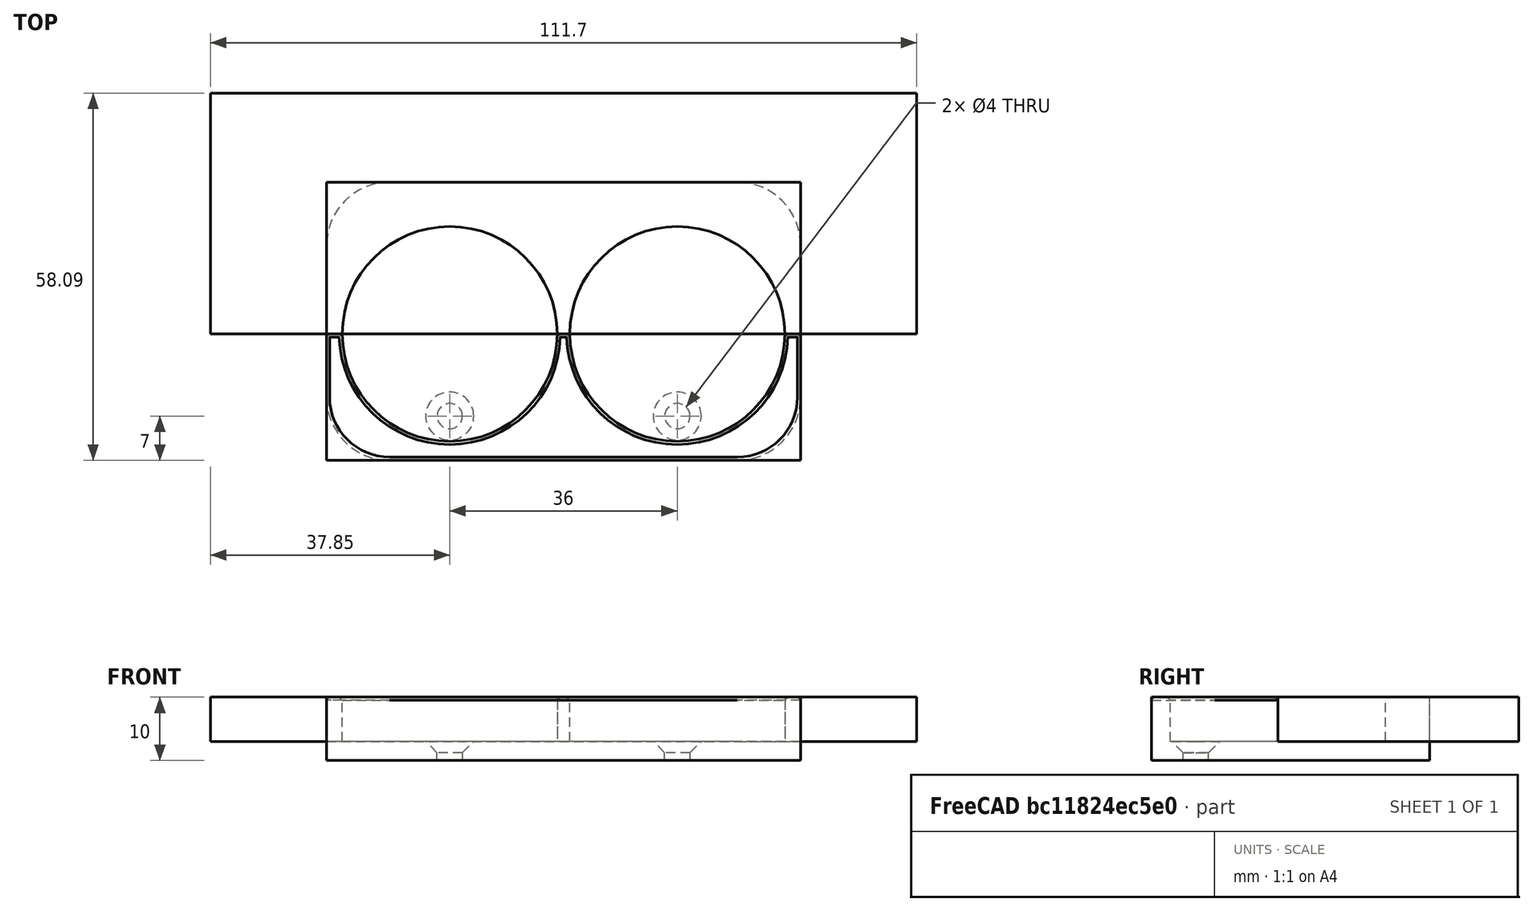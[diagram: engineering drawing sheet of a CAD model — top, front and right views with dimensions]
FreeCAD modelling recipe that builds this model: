
FCSTD DOCUMENT  (FreeCAD 0.16R)
Label: curtains2
License: All rights reserved
LicenseURL: http://en.wikipedia.org/wiki/All_rights_reserved
objects: Sketcher::SketchObject×4, PartDesign::Pocket×3, PartDesign::Chamfer×2, PartDesign::Pad×1, PartDesign::Fillet×1, Mesh::Feature×1
note: 15 computed .brp shape members not serialized (recipe doc carries the construction recipe); baked Part::Feature solids carry a one-line shape summary decoded from their .brp

FEATURE [Sketcher::SketchObject] Sketch
  sketch-geometry (4):
    g0: LineSegment StartX=-37.5 StartY=24 StartZ=0 EndX=37.5 EndY=24 EndZ=0
    g1: LineSegment StartX=37.5 StartY=24 StartZ=0 EndX=37.5 EndY=-20 EndZ=0
    g2: LineSegment StartX=37.5 StartY=-20 StartZ=0 EndX=-37.5 EndY=-20 EndZ=0
    g3: LineSegment StartX=-37.5 StartY=-20 StartZ=0 EndX=-37.5 EndY=24 EndZ=0
  constraints (12):
    c: Coincident(g0,g1)
    c: Coincident(g1,g2)
    c: Coincident(g2,g3)
    c: Coincident(g3,g0)
    c: Horizontal(g0)
    c: Horizontal(g2)
    c: Vertical(g1)
    c: Vertical(g3)
    c: DistanceY(g3,g3) = 44
    c: DistanceX(g0,g0) = 75
    c: DistanceY(g2) = -20
    c: Symmetric(g0,g0,g-2)
FEATURE [PartDesign::Pad] Pad
  Length = 10
  Length2 = 100
  Sketch = -> Sketch
  Type = 0
FEATURE [Sketcher::SketchObject] Sketch001
  Placement = pos=(0,0,10) rot=(0,0,1;0rad)
  Support = -> Pad [Face6]
  sketch-geometry (2):
    g0: Circle CenterX=-18 CenterY=0 CenterZ=0 NormalX=0 NormalY=0 NormalZ=1 Radius=17
    g1: Circle CenterX=18 CenterY=0 CenterZ=0 NormalX=0 NormalY=0 NormalZ=1 Radius=17
  constraints (6):
    c: Radius(g1) = 17
    c: Equal(g1,g0)
    c: PointOnObject(g0,g-1)
    c: PointOnObject(g1,g-1)
    c: Symmetric(g1,g0,g-1)
    c: DistanceX(g1) = 18
FEATURE [PartDesign::Pocket] Pocket
  Length = 7
  Sketch = -> Sketch001
  Type = 0
FEATURE [Sketcher::SketchObject] Sketch002
  Placement = pos=(0,0,10) rot=(0,0,1;0rad)
  Support = -> Pocket [Face5]
  sketch-geometry (4):
    g0: LineSegment StartX=-55.8545 StartY=38.0948 StartZ=0 EndX=55.8545 EndY=38.0948 EndZ=0
    g1: LineSegment StartX=55.8545 StartY=38.0948 StartZ=0 EndX=55.8545 EndY=0 EndZ=0
    g2: LineSegment StartX=55.8545 StartY=0 StartZ=0 EndX=-55.8545 EndY=0 EndZ=0
    g3: LineSegment StartX=-55.8545 StartY=0 StartZ=0 EndX=-55.8545 EndY=38.0948 EndZ=0
  constraints (12):
    c: Coincident(g0,g1)
    c: Coincident(g1,g2)
    c: Coincident(g2,g3)
    c: Coincident(g3,g0)
    c: Horizontal(g0)
    c: Horizontal(g2)
    c: Vertical(g1)
    c: Vertical(g3)
    c: PointOnObject(g1,g-1)
    c: Symmetric(g0,g0,g-2)
    c: DistanceY(g1,g1) = 38.0948
    c: DistanceX(g0,g0) = 111.709
FEATURE [PartDesign::Pocket] Pocket001
  Length = 7
  Sketch = -> Sketch002
  Type = 0
FEATURE [Sketcher::SketchObject] Sketch003
  ExternalGeometry = -> [Pocket001]
  Placement = pos=(0,0,10) rot=(0,0,1;0rad)
  Support = -> Pocket001 [Face7]
  sketch-geometry (2):
    g0: Circle CenterX=-18 CenterY=-13 CenterZ=0 NormalX=0 NormalY=0 NormalZ=1 Radius=2
    g1: Circle CenterX=18 CenterY=-13 CenterZ=0 NormalX=0 NormalY=0 NormalZ=1 Radius=2
  constraints (6):
    c: Radius(g0) = 2
    c: Equal(g0,g1)
    c: DistanceY(g0) = -13
    c: DistanceY(g1) = -13
    c: DistanceX(g0) = -18
    c: DistanceX(g1) = 18
FEATURE [PartDesign::Pocket] Pocket002
  Length = 5
  Sketch = -> Sketch003
  Type = 1
FEATURE [PartDesign::Fillet] Fillet
  Base = -> Pocket002 [Edge2,Edge4,Edge22,Edge10]
  Radius = 10
FEATURE [PartDesign::Chamfer] Chamfer
  Base = -> Fillet [Edge36,Edge38]
  Size = 1.8
FEATURE [PartDesign::Chamfer] Chamfer001
  Base = -> Chamfer [Edge25,Edge33,Edge47,Edge36,Edge48,Edge35,Edge49,Edge30,Edge41,Edge50]
  Size = 0.5
FEATURE [Mesh::Feature] Mesh  label="Chamfer001 (Meshed)"
